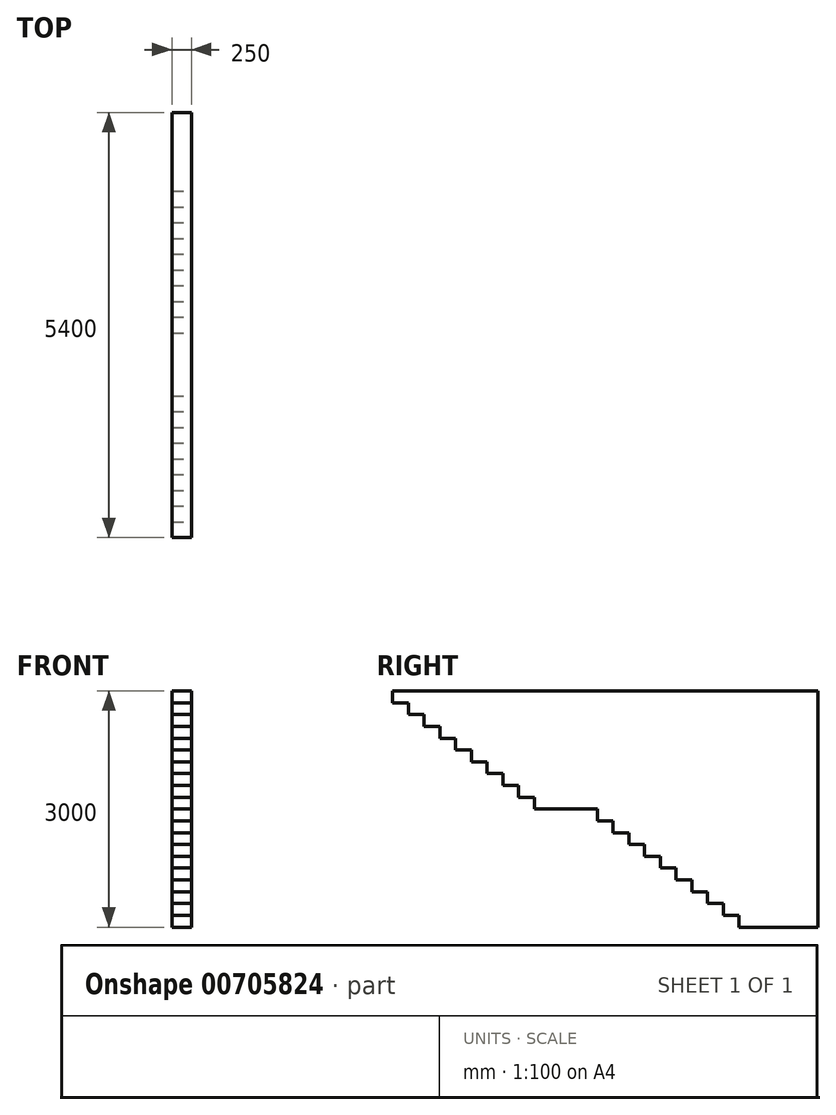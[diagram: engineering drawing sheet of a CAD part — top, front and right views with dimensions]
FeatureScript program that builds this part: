
annotation { "Feature Type Name" : "Feature", "Feature Type Description" : "" }
export const myFeature = defineFeature(function(context is Context, id is Id, definition is map)
    precondition{}
    {
        {
            var Q0;
            Q0=qCreatedBy(makeId("Right.planeOp"),FACE);
            var sketch = newSketch(context, id + "F0", { "sketchPlane" : qUnion([Q0])});
            skLineSegment(sketch, "E0.bottom", {"start": v(-66.15, 2951.76) * mm, "end": v(5333.85, 2951.76) * mm});
            skLineSegment(sketch, "E0.top", {"start": v(-66.15, -48.24) * mm, "end": v(5333.85, -48.24) * mm});
            skLineSegment(sketch, "E0.left", {"start": v(-66.15, 2951.76) * mm, "end": v(-66.15, -48.24) * mm});
            skLineSegment(sketch, "E0.right", {"start": v(5333.85, 2951.76) * mm, "end": v(5333.85, -48.24) * mm});
            skSolve(sketch);
        }
        {
            var Q0;
            Q0=makeQuery(id+"F0.imprint","IMPRINT",FACE,{"disambiguationData":[TD([[makeQuery(id+"F0.imprint","IMPRINT",EDGE,{"derivedFrom":sQuery(id+"F0.wireOp",EDGE,"E0.bottom")}),-1.0]])]});
            extrude(context, id + "F1", {"entities" : qUnion([Q0]), "depth" : 250 * mm, "offsetDistance" : 25 * mm});
        }
        {
            var Q0;
            Q0=makeQuery(id+"F1.opExtrude","CAP_FACE",FACE,{"disambiguationData":[OSD([sQuery(id+"F0.wireOp",EDGE,"E0.bottom"),sQuery(id+"F0.wireOp",EDGE,"E0.top"),sQuery(id+"F0.wireOp",EDGE,"E0.left"),sQuery(id+"F0.wireOp",EDGE,"E0.right")])],"isStart":false});
            var sketch = newSketch(context, id + "F2", { "sketchPlane" : qUnion([Q0])});
            skLineSegment(sketch, "E1", {"start": v(4333.85, -48.24) * mm, "end": v(4333.85, 101.76) * mm});
            skLineSegment(sketch, "E2", {"start": v(4333.85, 101.76) * mm, "end": v(4133.85, 101.76) * mm});
            skLineSegment(sketch, "E3", {"start": v(4133.85, 101.76) * mm, "end": v(4133.85, 251.76) * mm});
            skLineSegment(sketch, "E4", {"start": v(4133.85, 251.76) * mm, "end": v(3933.85, 251.76) * mm});
            skLineSegment(sketch, "E5", {"start": v(3933.85, 251.76) * mm, "end": v(3933.85, 401.76) * mm});
            skLineSegment(sketch, "E6", {"start": v(3933.85, 401.76) * mm, "end": v(3733.85, 401.76) * mm});
            skLineSegment(sketch, "E7", {"start": v(3733.85, 401.76) * mm, "end": v(3733.85, 551.76) * mm});
            skLineSegment(sketch, "E8", {"start": v(3733.85, 551.76) * mm, "end": v(3533.85, 551.76) * mm});
            skLineSegment(sketch, "E9", {"start": v(3533.85, 551.76) * mm, "end": v(3533.85, 701.76) * mm});
            skLineSegment(sketch, "E10", {"start": v(3533.85, 701.76) * mm, "end": v(3333.85, 701.76) * mm});
            skLineSegment(sketch, "E11", {"start": v(3333.85, 701.76) * mm, "end": v(3333.85, 851.76) * mm});
            skLineSegment(sketch, "E12", {"start": v(3333.85, 851.76) * mm, "end": v(3133.85, 851.76) * mm});
            skLineSegment(sketch, "E13", {"start": v(3133.85, 851.76) * mm, "end": v(3133.85, 1001.76) * mm});
            skLineSegment(sketch, "E14", {"start": v(3133.85, 1001.76) * mm, "end": v(2933.85, 1001.76) * mm});
            skLineSegment(sketch, "E15", {"start": v(2933.85, 1001.76) * mm, "end": v(2933.85, 1151.76) * mm});
            skLineSegment(sketch, "E16", {"start": v(2933.85, 1151.76) * mm, "end": v(2733.85, 1151.76) * mm});
            skLineSegment(sketch, "E17", {"start": v(2733.85, 1151.76) * mm, "end": v(2733.85, 1301.76) * mm});
            skLineSegment(sketch, "E18", {"start": v(2733.85, 1301.76) * mm, "end": v(2533.85, 1301.76) * mm});
            skLineSegment(sketch, "E19", {"start": v(2533.85, 1301.76) * mm, "end": v(2533.85, 1451.76) * mm});
            skLineSegment(sketch, "E20", {"start": v(2533.85, 1451.76) * mm, "end": v(1733.85, 1451.76) * mm});
            skLineSegment(sketch, "E21", {"start": v(1733.85, 1451.76) * mm, "end": v(1733.85, 1601.76) * mm});
            skLineSegment(sketch, "E22", {"start": v(1733.85, 1601.76) * mm, "end": v(1533.85, 1601.76) * mm});
            skLineSegment(sketch, "E23", {"start": v(1533.85, 1601.76) * mm, "end": v(1533.85, 1751.76) * mm});
            skLineSegment(sketch, "E24", {"start": v(1533.85, 1751.76) * mm, "end": v(1333.85, 1751.76) * mm});
            skLineSegment(sketch, "E25", {"start": v(1333.85, 1751.76) * mm, "end": v(1333.85, 1901.76) * mm});
            skLineSegment(sketch, "E26", {"start": v(1333.85, 1901.76) * mm, "end": v(1133.85, 1901.76) * mm});
            skLineSegment(sketch, "E27", {"start": v(1133.85, 1901.76) * mm, "end": v(1133.85, 2051.76) * mm});
            skLineSegment(sketch, "E28", {"start": v(1133.85, 2051.76) * mm, "end": v(933.85, 2051.76) * mm});
            skLineSegment(sketch, "E29", {"start": v(933.85, 2051.76) * mm, "end": v(933.85, 2201.76) * mm});
            skLineSegment(sketch, "E30", {"start": v(933.85, 2201.76) * mm, "end": v(733.85, 2201.76) * mm});
            skLineSegment(sketch, "E31", {"start": v(733.85, 2201.76) * mm, "end": v(733.85, 2351.76) * mm});
            skLineSegment(sketch, "E32", {"start": v(733.85, 2351.76) * mm, "end": v(533.85, 2351.76) * mm});
            skLineSegment(sketch, "E33", {"start": v(533.85, 2351.76) * mm, "end": v(533.85, 2501.76) * mm});
            skLineSegment(sketch, "E34", {"start": v(533.85, 2501.76) * mm, "end": v(333.85, 2501.76) * mm});
            skLineSegment(sketch, "E35", {"start": v(333.85, 2501.76) * mm, "end": v(333.85, 2651.76) * mm});
            skLineSegment(sketch, "E36", {"start": v(333.85, 2651.76) * mm, "end": v(133.85, 2651.76) * mm});
            skLineSegment(sketch, "E37", {"start": v(133.85, 2651.76) * mm, "end": v(133.85, 2801.76) * mm});
            skLineSegment(sketch, "E38", {"start": v(133.85, 2801.76) * mm, "end": v(-66.15, 2801.76) * mm});
            skLineSegment(sketch, "E39", {"start": v(-66.15, 2801.76) * mm, "end": v(-66.15, 2951.76) * mm});
            skSolve(sketch);
        }
        {
            var Q0;
            {var subQ0=sQuery(id+"F2.wireOp",EDGE,"E1");Q0=makeQuery(id+"F2.imprint","IMPRINT",FACE,{"disambiguationData":[TD([[makeQuery(id+"F2.imprint","IMPRINT",EDGE,{"derivedFrom":subQ0}),1.0]])]});}
            extrude(context, id + "F3", {"entities" : qUnion([Q0]), "operationType" : NewBodyOperationType.REMOVE, "oppositeDirection" : true, "depth" : 250 * mm, "offsetDistance" : 25 * mm});
        }
    });
